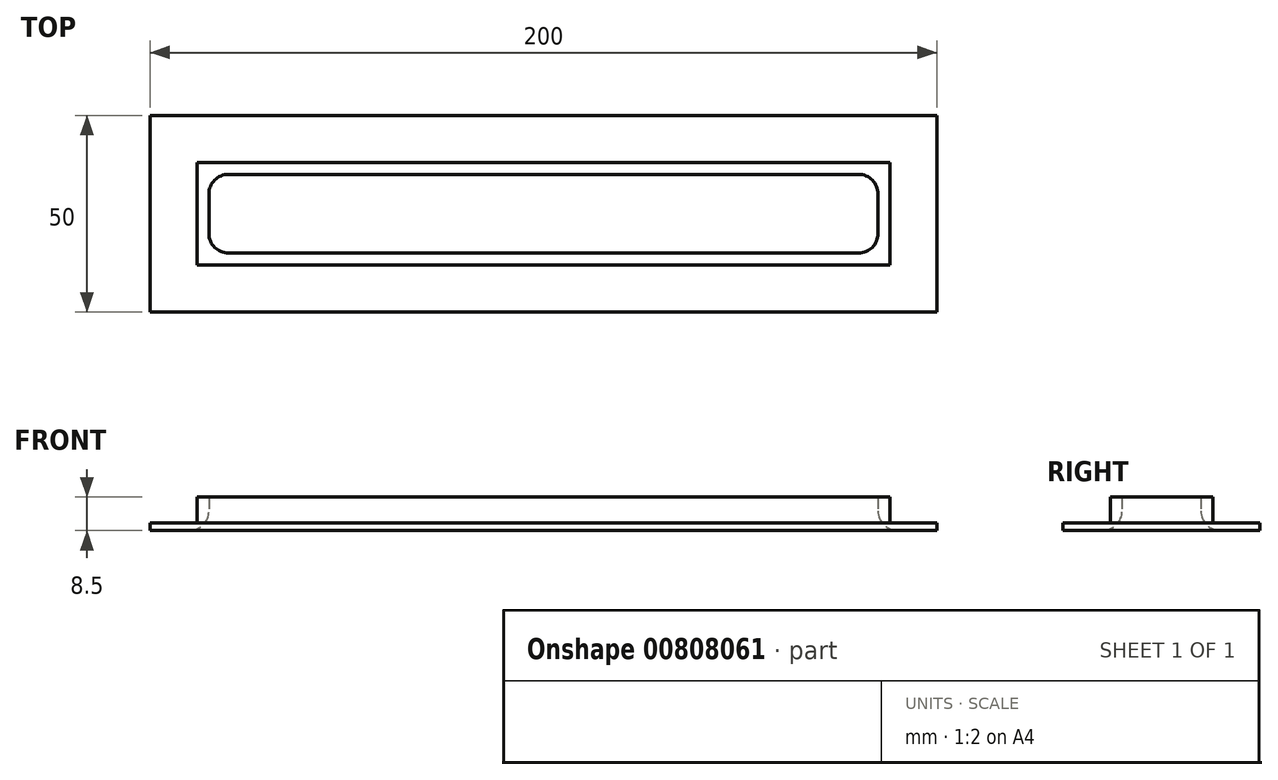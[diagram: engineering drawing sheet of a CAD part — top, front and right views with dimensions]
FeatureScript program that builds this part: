
annotation { "Feature Type Name" : "Feature", "Feature Type Description" : "" }
export const myFeature = defineFeature(function(context is Context, id is Id, definition is map)
    precondition{}
    {
        {
            var Q0;
            Q0=qCreatedBy(makeId("Top.planeOp"),FACE);
            var sketch = newSketch(context, id + "F0", { "sketchPlane" : qUnion([Q0])});
            skLineSegment(sketch, "E0.bottom", {"start": v(85, 10) * mm, "end": v(-85, 10) * mm});
            skLineSegment(sketch, "E0.top", {"start": v(85, -10) * mm, "end": v(-85, -10) * mm});
            skLineSegment(sketch, "E0.left", {"start": v(85, 10) * mm, "end": v(85, -10) * mm});
            skLineSegment(sketch, "E0.right", {"start": v(-85, 10) * mm, "end": v(-85, -10) * mm});
            skPoint(sketch, "E0.middle", {"position": v(0, 0) * mm});
            skLineSegment(sketch, "E1.bottom", {"start": v(88, 13) * mm, "end": v(-88, 13) * mm});
            skLineSegment(sketch, "E1.top", {"start": v(88, -13) * mm, "end": v(-88, -13) * mm});
            skLineSegment(sketch, "E1.left", {"start": v(88, 13) * mm, "end": v(88, -13) * mm});
            skLineSegment(sketch, "E1.right", {"start": v(-88, 13) * mm, "end": v(-88, -13) * mm});
            skLineSegment(sketch, "E2.bottom", {"start": v(100, 25) * mm, "end": v(-100, 25) * mm});
            skLineSegment(sketch, "E2.top", {"start": v(100, -25) * mm, "end": v(-100, -25) * mm});
            skLineSegment(sketch, "E2.left", {"start": v(100, 25) * mm, "end": v(100, -25) * mm});
            skLineSegment(sketch, "E2.right", {"start": v(-100, 25) * mm, "end": v(-100, -25) * mm});
            skSolve(sketch);
        }
        {
            var Q0;
            Q0=makeQuery(id+"F0.imprint","IMPRINT",FACE,{"disambiguationData":[TD([[makeQuery(id+"F0.imprint","IMPRINT",EDGE,{"derivedFrom":sQuery(id+"F0.wireOp",EDGE,"E0.bottom")}),-1.0]])]});
            var Q1;
            Q1=makeQuery(id+"F0.imprint","IMPRINT",FACE,{"disambiguationData":[TD([[makeQuery(id+"F0.imprint","IMPRINT",EDGE,{"derivedFrom":sQuery(id+"F0.wireOp",EDGE,"E1.bottom")}),-1.0]])]});
            extrude(context, id + "F1", {"entities" : qUnion([Q0, Q1]), "depth" : 2 * mm, "offsetDistance" : 25 * mm});
        }
        {
            var Q0;
            Q0=makeQuery(id+"F0.imprint","IMPRINT",FACE,{"disambiguationData":[TD([[makeQuery(id+"F0.imprint","IMPRINT",EDGE,{"derivedFrom":sQuery(id+"F0.wireOp",EDGE,"E0.bottom")}),-1.0]])]});
            extrude(context, id + "F2", {"entities" : qUnion([Q0]), "operationType" : NewBodyOperationType.ADD, "depth" : 8.5 * mm, "offsetDistance" : 25 * mm});
        }
        {
            var Q0;
            {var subQ0=sQuery(id+"F0.wireOp",EDGE,"E0.right");var subQ1=sQuery(id+"F0.wireOp",EDGE,"E0.top");Q0=makeQuery(id+"F2.boolean.opBoolean","MERGE",EDGE,{"derivedFrom":[makeQuery(id+"F1.opExtrude","SWEPT_EDGE",EDGE,{"disambiguationData":[OSD([subQ1,subQ0])]}),makeQuery(id+"F2.opExtrude","SWEPT_EDGE",EDGE,{"disambiguationData":[OSD([subQ1,subQ0])]})]});}
            var Q1;
            {var subQ0=sQuery(id+"F0.wireOp",EDGE,"E0.right");var subQ1=sQuery(id+"F0.wireOp",EDGE,"E0.bottom");Q1=makeQuery(id+"F2.boolean.opBoolean","MERGE",EDGE,{"derivedFrom":[makeQuery(id+"F1.opExtrude","SWEPT_EDGE",EDGE,{"disambiguationData":[OSD([subQ1,subQ0])]}),makeQuery(id+"F2.opExtrude","SWEPT_EDGE",EDGE,{"disambiguationData":[OSD([subQ1,subQ0])]})]});}
            var Q2;
            {var subQ0=sQuery(id+"F0.wireOp",EDGE,"E0.left");var subQ1=sQuery(id+"F0.wireOp",EDGE,"E0.top");Q2=makeQuery(id+"F2.boolean.opBoolean","MERGE",EDGE,{"derivedFrom":[makeQuery(id+"F1.opExtrude","SWEPT_EDGE",EDGE,{"disambiguationData":[OSD([subQ1,subQ0])]}),makeQuery(id+"F2.opExtrude","SWEPT_EDGE",EDGE,{"disambiguationData":[OSD([subQ1,subQ0])]})]});}
            var Q3;
            {var subQ0=sQuery(id+"F0.wireOp",EDGE,"E0.left");var subQ1=sQuery(id+"F0.wireOp",EDGE,"E0.bottom");Q3=makeQuery(id+"F2.boolean.opBoolean","MERGE",EDGE,{"derivedFrom":[makeQuery(id+"F1.opExtrude","SWEPT_EDGE",EDGE,{"disambiguationData":[OSD([subQ1,subQ0])]}),makeQuery(id+"F2.opExtrude","SWEPT_EDGE",EDGE,{"disambiguationData":[OSD([subQ1,subQ0])]})]});}
            fillet(context, id + "F3", {"entities" : qUnion([Q0, Q1, Q2, Q3]), "radius" : 5 * mm, "tangentPropagation" : true, "allowEdgeOverflow" : false});
        }
        {
            var Q0;
            Q0=makeQuery(id+"F1.opExtrude","CAP_EDGE",EDGE,{"disambiguationData":[OSD([sQuery(id+"F0.wireOp",EDGE,"E0.top")])],"isStart":true});
            fillet(context, id + "F4", {"entities" : qUnion([Q0]), "radius" : 5 * mm, "tangentPropagation" : true, "allowEdgeOverflow" : false});
        }
    });
